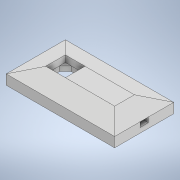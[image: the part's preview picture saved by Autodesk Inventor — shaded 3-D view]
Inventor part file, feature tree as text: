
AUTODESK INVENTOR PART (.ipt)
format: ipt  version: 2020 (Build 240168000, 168)  size: 258,560 bytes
history: native  units: mm
features: sketch x15, extrude x14
ambient origin geometry x8: Origin, YZ Plane, XZ Plane, XY Plane, X Axis, Y Axis, Z Axis, Center Point
bodies: Solid1 (feature_tree)
feature tree (29):
  extrude  "Extrusion1"  Depth=10.0mm
  extrude  "Extrusion2"  Depth=5.0mm
  extrude  "Extrusion3"  Depth=12.0mm
  extrude  "Extrusion4"  Depth=1.0mm
  extrude  "Extrusion5"  Depth=2.0mm TaperAngle=0.0deg
  extrude  "Extrusion6"  Depth=4.0mm
  extrude  "Extrusion7"  Depth=2.0mm
  extrude  "Extrusion8"  Depth=1.0mm TaperAngle=0.0deg
  extrude  "Extrusion9"  Depth=4.0mm
  extrude  "Extrusion10"  Depth=41.75mm TaperAngle=0.0deg
  extrude  "Extrusion11"  Depth=4.0mm
  extrude  "Extrusion12"  Depth=4.0mm TaperAngle=0.0deg
  extrude  "Extrusion13"  Depth=10.0mm
  extrude  "Extrusion14"  Depth=1.5mm TaperAngle=0.0deg
  sketch  "Sketch15"  dims[d41=26.0mm d42=0.0mm d43=3.997397mm d44=3.997397mm d45=17.75mm d46=0.0mm d47=17.75mm d48=0.0mm]
  sketch  "Sketch1"  dims[d0=10.0mm d1=10.0mm]
  sketch  "Sketch2"  dims[d2=5.0mm d3=5.0mm]
  sketch  "Sketch3"  dims[d4=12.0mm d5=12.0mm]
  sketch  "Sketch4"  dims[d6=1.0mm d7=1.0mm]
  sketch  "Sketch5"  dims[d8=2.0mm d9=0.0mm d10=11.5mm d11=0.0mm]
  sketch  "Sketch6"  dims[d13=4.0mm d14=4.0mm]
  sketch  "Sketch7"  dims[d15=2.0mm d16=2.0mm]
  sketch  "Sketch8"  dims[d17=23.25mm d18=0.0mm d19=1.0mm d20=0.0mm]
  sketch  "Sketch9"  dims[d21=25.0mm d22=0.0mm d23=4.0mm]
  sketch  "Sketch10"  dims[d24=23.25mm d25=0.0mm d26=41.75mm d27=0.0mm]
  sketch  "Sketch11"  dims[d28=11.625mm d29=0.0mm d30=4.0mm]
  sketch  "Sketch12"  dims[d31=4.0mm d32=105.0mm d33=0.0mm]
  sketch  "Sketch13"  dims[d34=10.0mm d35=0.0mm d36=10.0mm]
  sketch  "Sketch14"  dims[d37=4.25mm d38=0.0mm d39=1.5mm d40=0.0mm]
